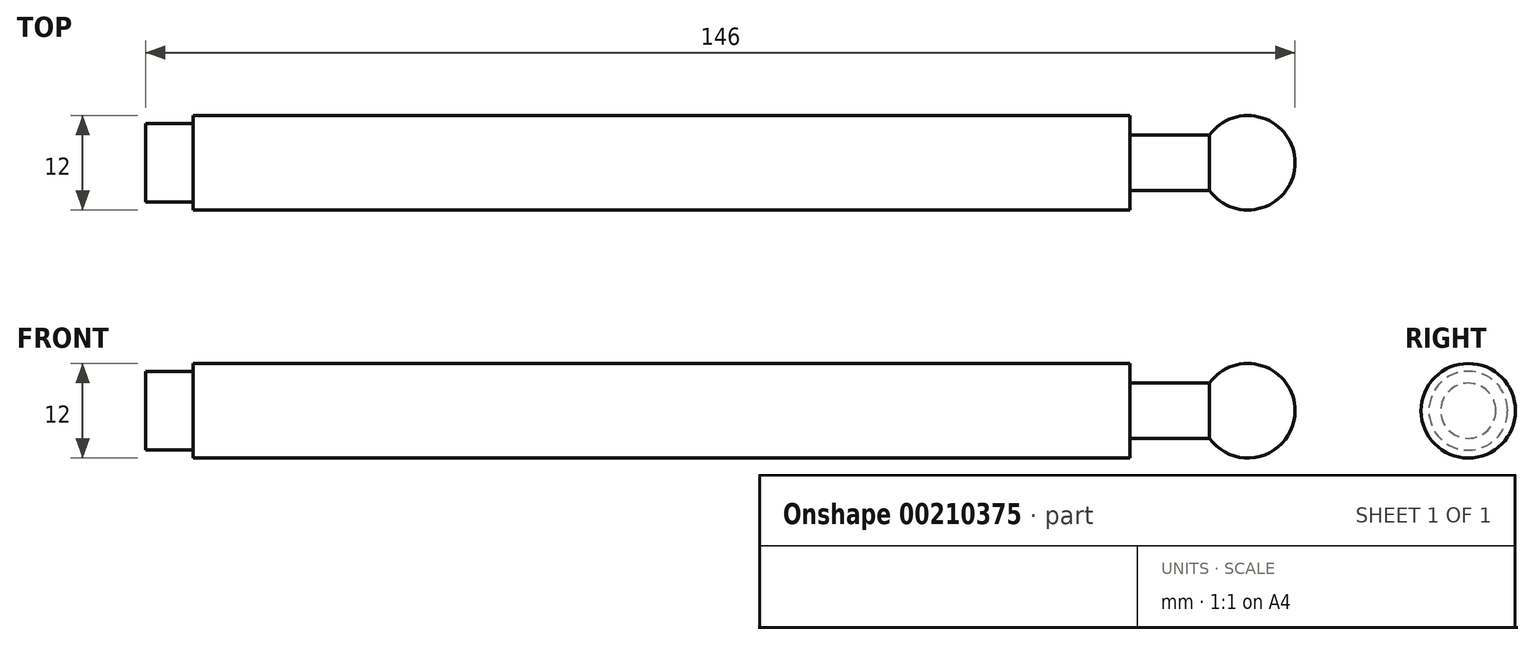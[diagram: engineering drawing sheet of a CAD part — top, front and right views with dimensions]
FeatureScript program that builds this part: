
annotation { "Feature Type Name" : "Feature", "Feature Type Description" : "" }
export const myFeature = defineFeature(function(context is Context, id is Id, definition is map)
    precondition{}
    {
        {
            var Q0;
            Q0=qCreatedBy(makeId("Right.planeOp"),FACE);
            var sketch = newSketch(context, id + "F0", { "sketchPlane" : qUnion([Q0])});
            skCircle(sketch, "E0", {"center": v(0, 0) * mm, "radius": 6 * mm});
            skSolve(sketch);
        }
        {
            var Q0;
            Q0 = qSketchRegion(id + "F0", true);
            extrude(context, id + "F1", {"entities" : qUnion([Q0]), "depth" : 119 * mm});
        }
        {
            var Q0;
            Q0=makeQuery(id+"F1.opExtrude","CAP_FACE",FACE,{"disambiguationData":[OSD([sQuery(id+"F0.wireOp",EDGE,"E0")])],"isStart":true});
            var sketch = newSketch(context, id + "F2", { "sketchPlane" : qUnion([Q0])});
            skCircle(sketch, "E1", {"center": v(0, 0) * mm, "radius": 5 * mm});
            skSolve(sketch);
        }
        {
            var Q0;
            Q0 = qSketchRegion(id + "F2", true);
            extrude(context, id + "F3", {"entities" : qUnion([Q0]), "operationType" : NewBodyOperationType.ADD, "depth" : 6 * mm});
        }
        {
            var Q0;
            Q0=makeQuery(id+"F1.opExtrude","CAP_FACE",FACE,{"disambiguationData":[OSD([sQuery(id+"F0.wireOp",EDGE,"E0")])],"isStart":false});
            var sketch = newSketch(context, id + "F4", { "sketchPlane" : qUnion([Q0])});
            skCircle(sketch, "E2", {"center": v(0, 0) * mm, "radius": 3.5 * mm});
            skSolve(sketch);
        }
        {
            var Q0;
            Q0 = qSketchRegion(id + "F4", true);
            extrude(context, id + "F5", {"entities" : qUnion([Q0]), "operationType" : NewBodyOperationType.ADD, "depth" : 10.13 * mm});
        }
        {
            var Q0;
            Q0=qCreatedBy(makeId("Front.planeOp"),FACE);
            var sketch = newSketch(context, id + "F6", { "sketchPlane" : qUnion([Q0])});
            skArc(sketch, "E3", {"start": v(140, 0) * mm, "mid": v(134, 6) * mm, "end": v(128, 0) * mm});
            skLineSegment(sketch, "E4", {"start": v(128, 0) * mm, "end": v(140, 0) * mm});
            skSolve(sketch);
        }
        {
            var Q0;
            Q0 = qSketchRegion(id + "F6", true);
            var Q1;
            Q1=sQuery(id+"F6.wireOp",EDGE,"E4");
            revolve(context, id + "F7", {"operationType" : NewBodyOperationType.ADD, "entities" : qUnion([Q0]), "axis" : qUnion([Q1]), "revolveType" : RevolveType.FULL});
        }
    });
